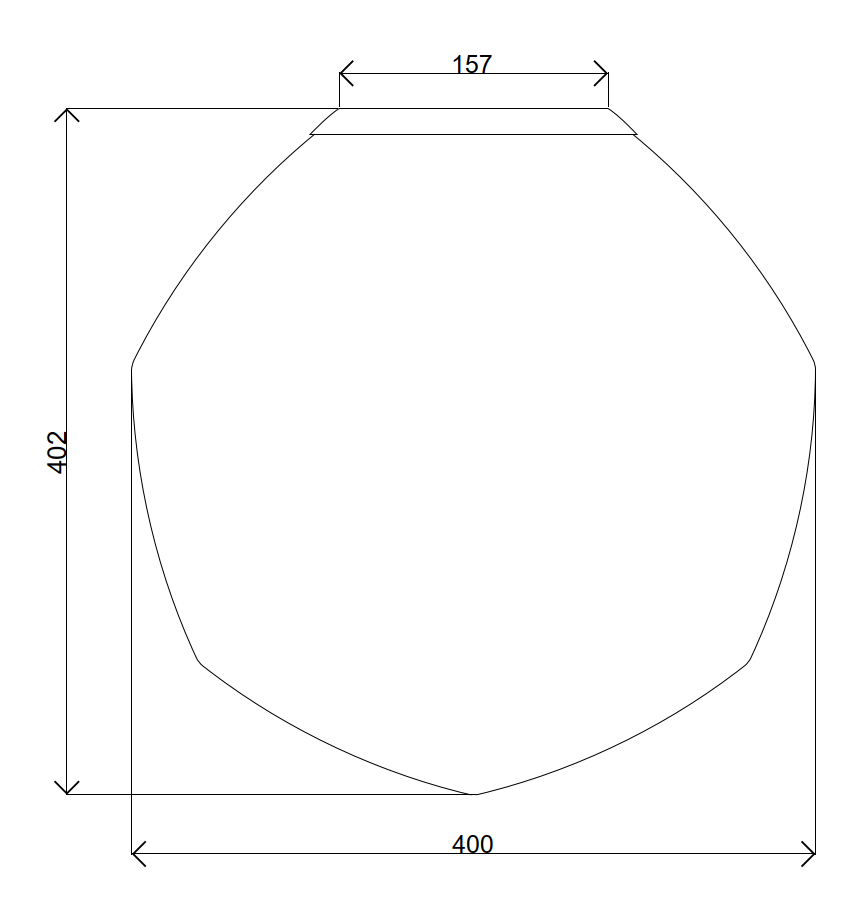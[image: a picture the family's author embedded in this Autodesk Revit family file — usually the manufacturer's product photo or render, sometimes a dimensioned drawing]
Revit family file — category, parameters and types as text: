
# Revit family: 63_UN_Pendant_Cloak Track_Signify
name_source: partatom
category: Lighting Fixtures
units: mm (PartAtom-declared; Revit-internal decimal feet)

## family parameters
Always vertical = Yes
Cut with Voids When Loaded = No
Light Source = Yes
OmniClass Number = 23.80.70.11
OmniClass Title = Luminaries for Internal Lighting
Part Type = Normal
Room Calculation Point = Yes
Round Connector Dimension = Use Diameter
Shared = No
Work Plane-Based = No

## types (1)
- Cloak Track
    Apparent Load = 10 VA
    Assembly Code = 63.0
    Color Filter = 16777215
    Dimming Lamp Color Temperature Shift = <None>
    IfcExportAs = IfcLightFixtureType
    IfcExportType = USERDEFINED
    Lamp = LED
    Light Source Symbol Size = 610 mm
    Manufacturer = Signify
    Model = Pendant Track
    Pendant_Material = UHMW, White
    Type Comments = Cloak
    URL = https://www.signify.com
    Voltage = 230 V
    Wattage Comments = 10W

## geometry (parser evidence)
native form markers: Sweep x7
no freeform markers — native parametric forms only
